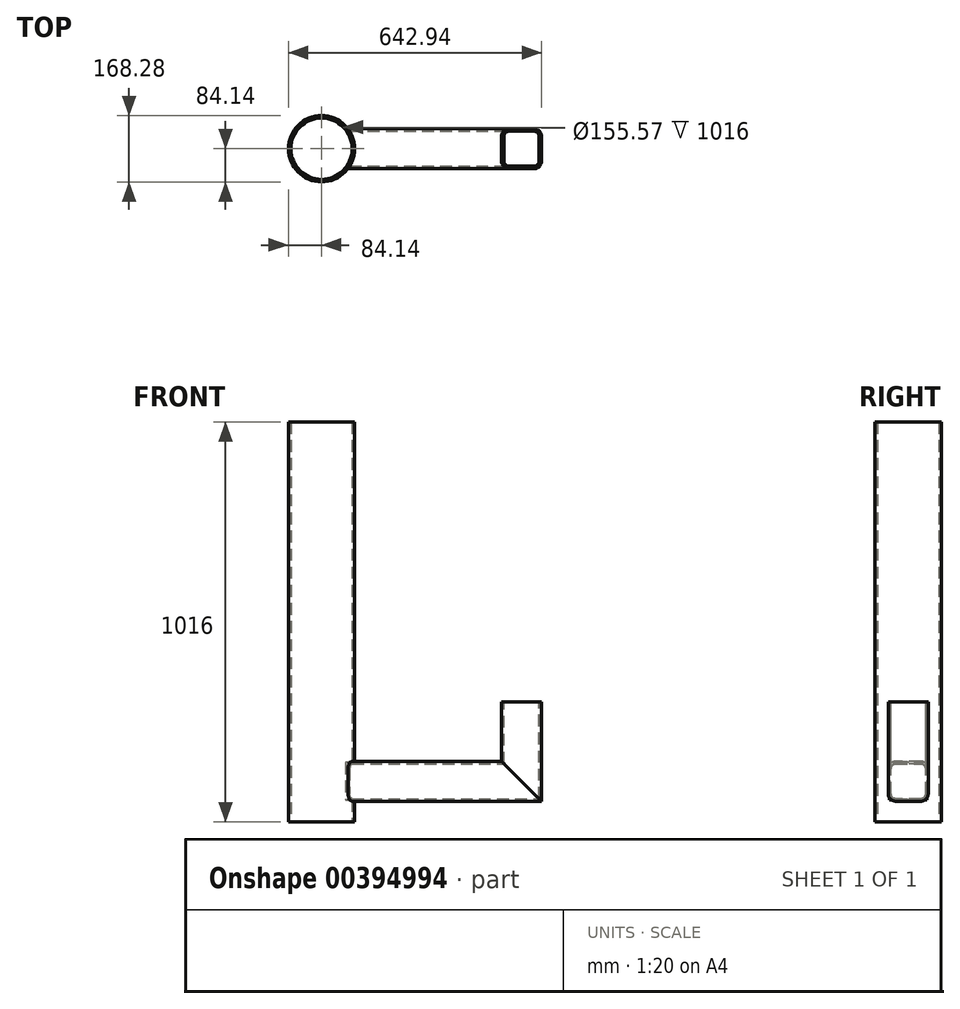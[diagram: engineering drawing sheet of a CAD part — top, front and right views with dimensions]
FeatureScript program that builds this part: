
annotation { "Feature Type Name" : "Feature", "Feature Type Description" : "" }
export const myFeature = defineFeature(function(context is Context, id is Id, definition is map)
    precondition{}
    {
        {
            var Q0;
            Q0=qCreatedBy(makeId("Top.planeOp"),FACE);
            var sketch = newSketch(context, id + "F0", { "sketchPlane" : qUnion([Q0])});
            skCircle(sketch, "E0", {"center": v(0, 0) * mm, "radius": 84.14 * mm});
            skCircle(sketch, "E1", {"center": v(0, 0) * mm, "radius": 77.79 * mm});
            skSolve(sketch);
        }
        {
            var Q0;
            Q0=makeQuery(id+"F0.imprint","IMPRINT",FACE,{"disambiguationData":[TD([[makeQuery(id+"F0.imprint","IMPRINT",EDGE,{"derivedFrom":sQuery(id+"F0.wireOp",EDGE,"E0")}),1.0]])]});
            extrude(context, id + "F1", {"entities" : qUnion([Q0]), "depth" : 1016 * mm});
        }
        {
            var Q0;
            Q0=qCreatedBy(makeId("Right.planeOp"),FACE);
            var sketch = newSketch(context, id + "F2", { "sketchPlane" : qUnion([Q0])});
            skLineSegment(sketch, "E2.bottom", {"start": v(47.63, 55.56) * mm, "end": v(-47.62, 55.56) * mm});
            skLineSegment(sketch, "E2.top", {"start": v(47.62, 150.81) * mm, "end": v(-47.63, 150.81) * mm});
            skLineSegment(sketch, "E2.left", {"start": v(47.63, 55.56) * mm, "end": v(47.62, 150.81) * mm});
            skLineSegment(sketch, "E2.right", {"start": v(-47.62, 55.56) * mm, "end": v(-47.63, 150.81) * mm});
            skPoint(sketch, "E2.middle", {"position": v(0, 103.19) * mm});
            skSolve(sketch);
        }
        {
            var Q0;
            Q0=makeQuery(id+"F2.imprint","IMPRINT",FACE,{"disambiguationData":[TD([[makeQuery(id+"F2.imprint","IMPRINT",EDGE,{"derivedFrom":sQuery(id+"F2.wireOp",EDGE,"E2.bottom")}),-1.0]])]});
            extrude(context, id + "F3", {"entities" : qUnion([Q0]), "operationType" : NewBodyOperationType.REMOVE, "endBound" : BoundingType.THROUGH_ALL, "depth" : 25.4 * mm});
        }
        {
            var Q0;
            Q0=qCreatedBy(makeId("Right.planeOp"),FACE);
            cPlane(context, id + "F4", {"entities" : qUnion([Q0]), "cplaneType" : CPlaneType.OFFSET, "offset" : 558.8 * mm, "width" : 152.4 * mm, "height" : 152.4 * mm});
        }
        {
            var Q0;
            Q0=qCreatedBy(id+"F4.planeOp",FACE);
            var sketch = newSketch(context, id + "F5", { "sketchPlane" : qUnion([Q0])});
            skLineSegment(sketch, "E3.bottom", {"start": v(31.75, 52.39) * mm, "end": v(-31.75, 52.39) * mm});
            skLineSegment(sketch, "E3.top", {"start": v(31.75, 153.99) * mm, "end": v(-31.75, 153.99) * mm});
            skLineSegment(sketch, "E3.left", {"start": v(50.8, 71.44) * mm, "end": v(50.8, 134.94) * mm});
            skLineSegment(sketch, "E3.right", {"start": v(-50.8, 71.44) * mm, "end": v(-50.8, 134.94) * mm});
            skPoint(sketch, "E3.middle", {"position": v(0, 103.19) * mm});
            skPoint(sketch, "E4.visualSharp", {"position": v(-50.8, 153.99) * mm});
            skArc(sketch, "E4.filletArc", {"start": v(-31.75, 153.99) * mm, "mid": v(-45.22, 148.4) * mm, "end": v(-50.8, 134.94) * mm});
            skPoint(sketch, "E5.visualSharp", {"position": v(50.8, 153.99) * mm});
            skArc(sketch, "E5.filletArc", {"start": v(50.8, 134.94) * mm, "mid": v(45.22, 148.4) * mm, "end": v(31.75, 153.99) * mm});
            skPoint(sketch, "E6.visualSharp", {"position": v(50.8, 52.39) * mm});
            skArc(sketch, "E6.filletArc", {"start": v(31.75, 52.39) * mm, "mid": v(45.22, 57.97) * mm, "end": v(50.8, 71.44) * mm});
            skPoint(sketch, "E7.visualSharp", {"position": v(-50.8, 52.39) * mm});
            skArc(sketch, "E7.filletArc", {"start": v(-50.8, 71.44) * mm, "mid": v(-45.22, 57.97) * mm, "end": v(-31.75, 52.39) * mm});
            skArc(sketch, "E8.0", {"start": v(44.45, 134.94) * mm, "mid": v(40.73, 143.92) * mm, "end": v(31.75, 147.64) * mm});
            skLineSegment(sketch, "E8.1", {"start": v(44.45, 71.44) * mm, "end": v(44.45, 134.94) * mm});
            skLineSegment(sketch, "E8.2", {"start": v(31.75, 147.64) * mm, "end": v(-31.75, 147.64) * mm});
            skArc(sketch, "E8.3", {"start": v(31.75, 58.74) * mm, "mid": v(40.73, 62.46) * mm, "end": v(44.45, 71.44) * mm});
            skArc(sketch, "E8.4", {"start": v(-31.75, 147.64) * mm, "mid": v(-40.73, 143.92) * mm, "end": v(-44.45, 134.94) * mm});
            skLineSegment(sketch, "E8.5", {"start": v(-44.45, 71.44) * mm, "end": v(-44.45, 134.94) * mm});
            skArc(sketch, "E8.6", {"start": v(-44.45, 71.44) * mm, "mid": v(-40.73, 62.46) * mm, "end": v(-31.75, 58.74) * mm});
            skLineSegment(sketch, "E8.7", {"start": v(31.75, 58.74) * mm, "end": v(-31.75, 58.74) * mm});
            skSolve(sketch);
        }
        {
            var Q0;
            Q0=makeQuery(id+"F5.imprint","IMPRINT",FACE,{"disambiguationData":[TD([[makeQuery(id+"F5.imprint","IMPRINT",EDGE,{"derivedFrom":sQuery(id+"F5.wireOp",EDGE,"E3.bottom")}),-1.0]])]});
            var Q1;
            Q1=makeQuery(id+"F1.opExtrude","SWEPT_FACE",FACE,{"disambiguationData":[OSD([sQuery(id+"F0.wireOp",EDGE,"E0")])]});
            extrude(context, id + "F6", {"entities" : qUnion([Q0]), "endBound" : BoundingType.UP_TO_SURFACE, "oppositeDirection" : true, "endBoundEntityFace" : qUnion([Q1]), "depth" : 25.4 * mm});
        }
        {
            var Q0;
            Q0=qCreatedBy(makeId("Top.planeOp"),FACE);
            cPlane(context, id + "F7", {"entities" : qUnion([Q0]), "cplaneType" : CPlaneType.OFFSET, "offset" : 304.8 * mm, "width" : 152.4 * mm, "height" : 152.4 * mm});
        }
        {
            var Q0;
            Q0=qCreatedBy(id+"F7.planeOp",FACE);
            var sketch = newSketch(context, id + "F8", { "sketchPlane" : qUnion([Q0])});
            skLineSegment(sketch, "E9.bottom", {"start": v(539.75, 50.8) * mm, "end": v(476.25, 50.8) * mm});
            skLineSegment(sketch, "E9.top", {"start": v(539.75, -50.8) * mm, "end": v(476.25, -50.8) * mm});
            skLineSegment(sketch, "E9.left", {"start": v(558.8, 31.75) * mm, "end": v(558.8, -31.75) * mm});
            skLineSegment(sketch, "E9.right", {"start": v(457.2, 31.75) * mm, "end": v(457.2, -31.75) * mm});
            skPoint(sketch, "E9.middle", {"position": v(508, 0) * mm});
            skPoint(sketch, "E10.visualSharp", {"position": v(457.2, 50.8) * mm});
            skArc(sketch, "E10.filletArc", {"start": v(476.25, 50.8) * mm, "mid": v(462.78, 45.22) * mm, "end": v(457.2, 31.75) * mm});
            skPoint(sketch, "E11.visualSharp", {"position": v(558.8, 50.8) * mm});
            skArc(sketch, "E11.filletArc", {"start": v(558.8, 31.75) * mm, "mid": v(553.22, 45.22) * mm, "end": v(539.75, 50.8) * mm});
            skPoint(sketch, "E12.visualSharp", {"position": v(558.8, -50.8) * mm});
            skArc(sketch, "E12.filletArc", {"start": v(539.75, -50.8) * mm, "mid": v(553.22, -45.22) * mm, "end": v(558.8, -31.75) * mm});
            skPoint(sketch, "E13.visualSharp", {"position": v(457.2, -50.8) * mm});
            skArc(sketch, "E13.filletArc", {"start": v(457.2, -31.75) * mm, "mid": v(462.78, -45.22) * mm, "end": v(476.25, -50.8) * mm});
            skArc(sketch, "E14.0", {"start": v(552.45, 31.75) * mm, "mid": v(548.73, 40.73) * mm, "end": v(539.75, 44.45) * mm});
            skLineSegment(sketch, "E14.1", {"start": v(552.45, 31.75) * mm, "end": v(552.45, -31.75) * mm});
            skLineSegment(sketch, "E14.2", {"start": v(539.75, 44.45) * mm, "end": v(476.25, 44.45) * mm});
            skArc(sketch, "E14.3", {"start": v(539.75, -44.45) * mm, "mid": v(548.73, -40.73) * mm, "end": v(552.45, -31.75) * mm});
            skArc(sketch, "E14.4", {"start": v(476.25, 44.45) * mm, "mid": v(467.27, 40.73) * mm, "end": v(463.55, 31.75) * mm});
            skLineSegment(sketch, "E14.5", {"start": v(463.55, 31.75) * mm, "end": v(463.55, -31.75) * mm});
            skArc(sketch, "E14.6", {"start": v(463.55, -31.75) * mm, "mid": v(467.27, -40.73) * mm, "end": v(476.25, -44.45) * mm});
            skLineSegment(sketch, "E14.7", {"start": v(539.75, -44.45) * mm, "end": v(476.25, -44.45) * mm});
            skSolve(sketch);
        }
        {
            var Q0;
            Q0=makeQuery(id+"F6.opExtrude","SWEPT_FACE",FACE,{"disambiguationData":[OSD([sQuery(id+"F5.wireOp",EDGE,"E3.right")])]});
            var sketch = newSketch(context, id + "F9", { "sketchPlane" : qUnion([Q0])});
            skLineSegment(sketch, "E15", {"start": v(457.2, 153.99) * mm, "end": v(558.8, 52.39) * mm});
            skLineSegment(sketch, "E16", {"start": v(457.2, 153.99) * mm, "end": v(558.8, 153.99) * mm});
            skLineSegment(sketch, "E17", {"start": v(558.8, 153.99) * mm, "end": v(558.8, 52.39) * mm});
            skSolve(sketch);
        }
        {
            var Q0;
            {var subQ0=sQuery(id+"F9.wireOp",EDGE,"E16");Q0=makeQuery(id+"F9.imprint","IMPRINT",FACE,{"disambiguationData":[TD([[makeQuery(id+"F9.imprint","IMPRINT",EDGE,{"derivedFrom":subQ0}),-1.0]])]});}
            var Q1;
            {var subQ0=sQuery(id+"F9.wireOp",EDGE,"E15");var subQ1=sQuery(id+"F5.wireOp",EDGE,"E3.right");var subQ2=makeQuery(id+"F6.opExtrude","SWEPT_EDGE",EDGE,{"disambiguationData":[OSD([subQ1,sQuery(id+"F5.wireOp",EDGE,"E4.filletArc")])]});var subQ3=makeQuery(id+"F9.imprint","INTERSECT",VERTEX,{"derivedFrom":[subQ2,subQ0]});Q1=makeQuery(id+"F9.imprint","IMPRINT",FACE,{"disambiguationData":[TD([[makeQuery(id+"F9.imprint","IMPRINT",EDGE,{"disambiguationData":[TD([[subQ3,-1.0]])],"derivedFrom":subQ0}),1.0]])]});}
            var Q2;
            {var subQ0=sQuery(id+"F9.wireOp",EDGE,"E17");var subQ1=sQuery(id+"F9.wireOp",EDGE,"E15");var subQ2=makeQuery(id+"F9.imprint","INTERSECT",VERTEX,{"derivedFrom":[subQ1,subQ0]});Q2=makeQuery(id+"F9.imprint","IMPRINT",FACE,{"disambiguationData":[TD([[makeQuery(id+"F9.imprint","IMPRINT",EDGE,{"disambiguationData":[TD([[subQ2,1.0]])],"derivedFrom":subQ1}),1.0]])]});}
            extrude(context, id + "F10", {"entities" : qUnion([Q0, Q1, Q2]), "operationType" : NewBodyOperationType.REMOVE, "endBound" : BoundingType.THROUGH_ALL, "oppositeDirection" : true, "depth" : 25.4 * mm});
        }
        {
            var Q0;
            Q0=makeQuery(id+"F8.imprint","IMPRINT",FACE,{"disambiguationData":[TD([[makeQuery(id+"F8.imprint","IMPRINT",EDGE,{"derivedFrom":sQuery(id+"F8.wireOp",EDGE,"E9.bottom")}),1.0]])]});
            extrude(context, id + "F11", {"entities" : qUnion([Q0]), "endBound" : BoundingType.UP_TO_NEXT, "oppositeDirection" : true, "depth" : 25.4 * mm});
        }
    });
